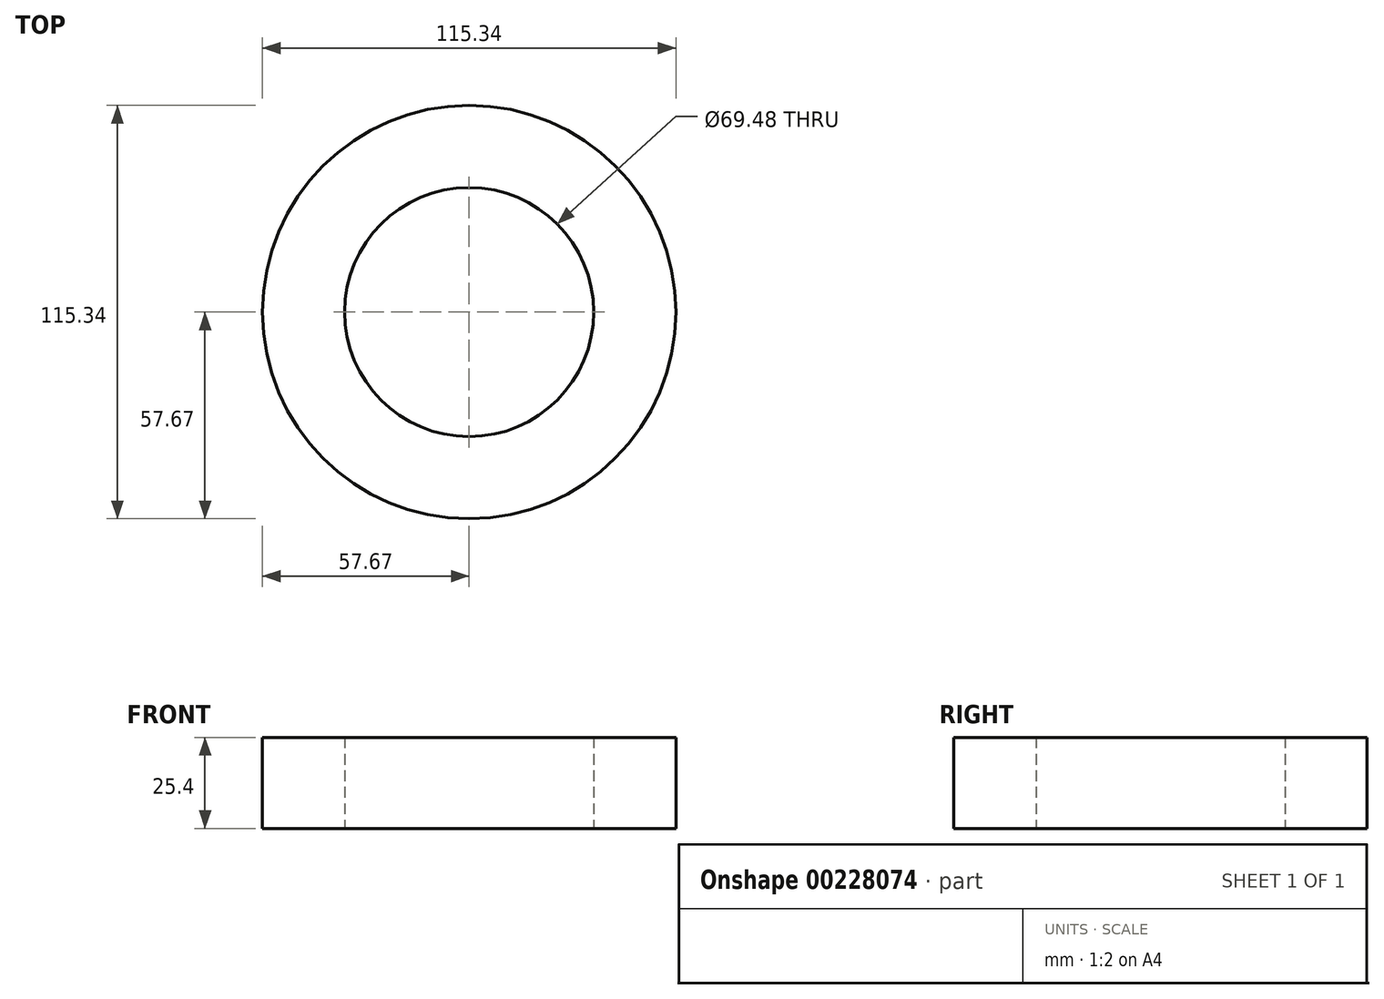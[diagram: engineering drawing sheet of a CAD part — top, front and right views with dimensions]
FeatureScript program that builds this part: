
annotation { "Feature Type Name" : "Feature", "Feature Type Description" : "" }
export const myFeature = defineFeature(function(context is Context, id is Id, definition is map)
    precondition{}
    {
        {
            var Q0;
            Q0=qCreatedBy(makeId("Top.planeOp"),FACE);
            var sketch = newSketch(context, id + "F0", { "sketchPlane" : qUnion([Q0])});
            skCircle(sketch, "E0", {"center": v(0, 0) * mm, "radius": 57.67 * mm});
            skCircle(sketch, "E1", {"center": v(0, 0) * mm, "radius": 34.74 * mm});
            skSolve(sketch);
        }
        {
            var Q0;
            Q0=makeQuery(id+"F0.imprint","IMPRINT",FACE,{"disambiguationData":[TD([[makeQuery(id+"F0.imprint","IMPRINT",EDGE,{"derivedFrom":sQuery(id+"F0.wireOp",EDGE,"E0")}),1.0]])]});
            extrude(context, id + "F1", {"entities" : qUnion([Q0]), "depth" : 25.4 * mm});
        }
    });
